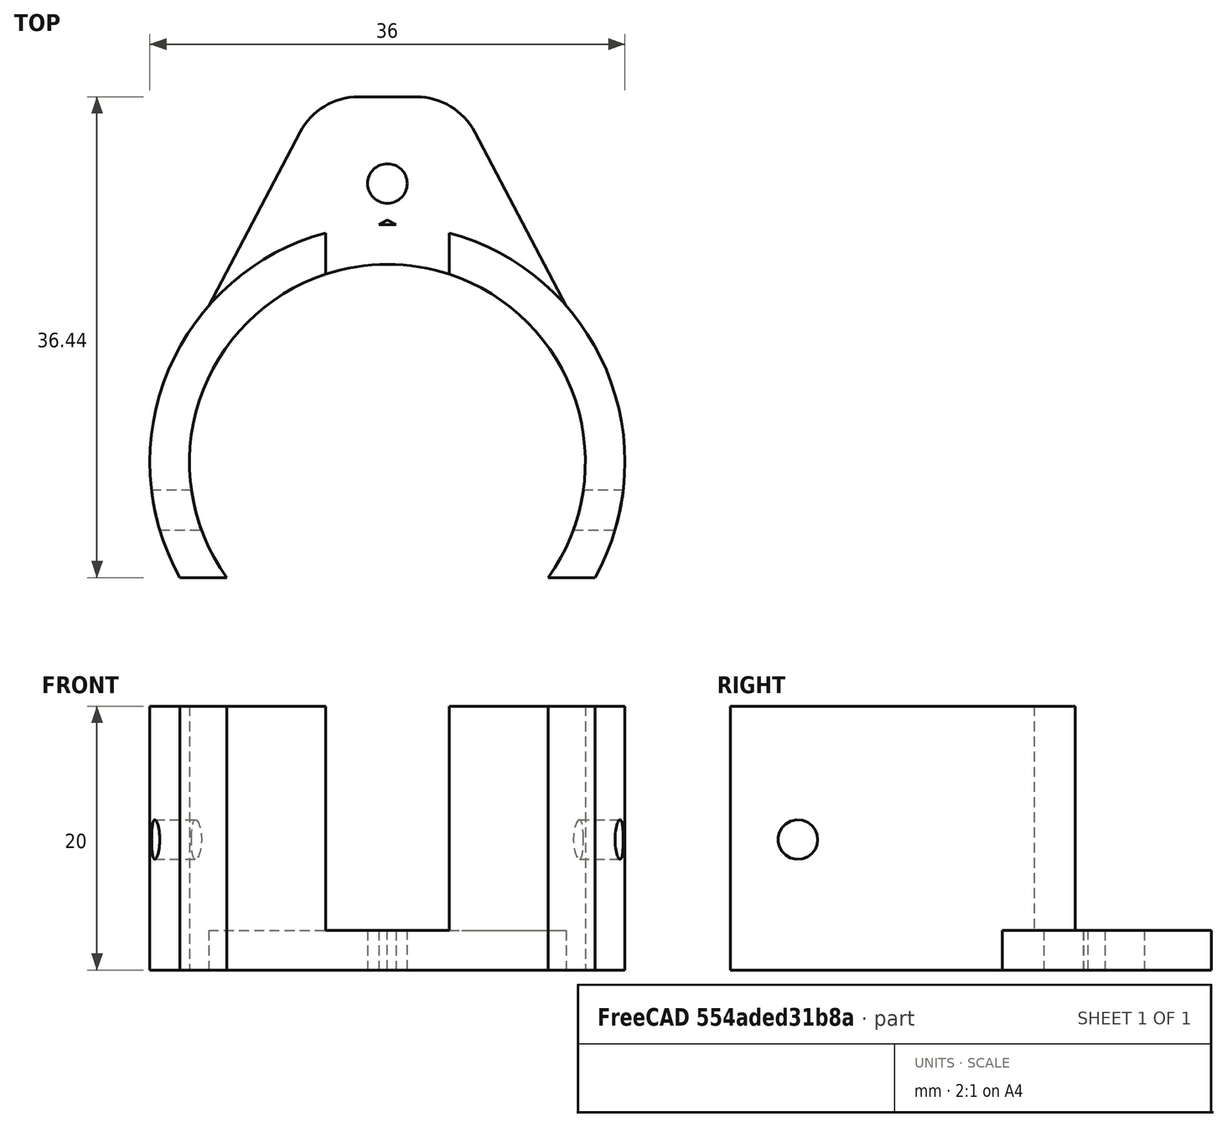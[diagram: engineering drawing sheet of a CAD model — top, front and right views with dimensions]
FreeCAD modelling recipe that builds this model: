
FCSTD DOCUMENT  (FreeCAD 0.19R24366 (Git))
Label: spool holder
License: All rights reserved
LicenseURL: http://en.wikipedia.org/wiki/All_rights_reserved
objects: Sketcher::SketchObject×5, PartDesign::Pocket×3, PartDesign::Pad×2, PartDesign::Fillet×2, Mesh::Feature×1, PartDesign::Body×1
note: 20 computed .brp shape members not serialized (recipe doc carries the construction recipe); baked Part::Feature solids carry a one-line shape summary decoded from their .brp

FEATURE [Mesh::Feature] spoolStand
FEATURE [Sketcher::SketchObject] Sketch
  FullyConstrained = false
  MapMode = 5
  Support = -> [XY_Plane]
  sketch-geometry (6):
    g0: ArcOfCircle CenterX=0 CenterY=3.63926 CenterZ=0 NormalX=0 NormalY=0 NormalZ=1 AngleXU=0 Radius=15 StartAngle=5.66017 EndAngle=10.0478
    g1: ArcOfCircle CenterX=0 CenterY=3.63926 CenterZ=0 NormalX=0 NormalY=0 NormalZ=1 AngleXU=0 Radius=18 StartAngle=5.7754 EndAngle=9.93256
    g2: LineSegment StartX=-15.7288 StartY=-5.11309 StartZ=0 EndX=-12.1818 EndY=-5.11309 EndZ=0
    g3: GeomPoint X=-12.1762 Y=-5.11309 Z=0
    g4: GeomPoint X=12.1761 Y=-5.11309 Z=0
    g5: LineSegment StartX=12.1818 StartY=-5.11309 StartZ=0 EndX=15.7288 EndY=-5.11309 EndZ=0
  constraints (11):
    c: PointOnObject(g0,g-2)
    c: Radius(g0) = 15
    c: Coincident(g1,g0)
    c: Horizontal(g2)
    c: PointOnObject(g3,g2)
    c: PointOnObject(g4,g2)
    c: Coincident(g1,g5)
    c: Coincident(g1,g2)
    c: Coincident(g2,g0)
    c: Coincident(g5,g0)
    c: Tangent(g2,g5)
FEATURE [PartDesign::Pad] Pad
  Direction = (1,1,1)
  Length = 20
  Length2 = 100
  Profile = -> Sketch
  Type = 0
FEATURE [Sketcher::SketchObject] Sketch002
  AttachmentOffset = pos=(0,0,3) rot=(0,0,1;0rad)
  FullyConstrained = false
  MapMode = 5
  Placement = pos=(0,0,3) rot=(0,0,1;0rad)
  Support = -> [XY_Plane]
  sketch-geometry (4):
    g0: LineSegment StartX=-4.69492 StartY=22 StartZ=0 EndX=4.69492 EndY=22 EndZ=0
    g1: LineSegment StartX=4.69492 StartY=22 StartZ=0 EndX=4.69492 EndY=16.8424 EndZ=0
    g2: LineSegment StartX=4.69492 StartY=16.8424 StartZ=0 EndX=-4.69492 EndY=16.8424 EndZ=0
    g3: LineSegment StartX=-4.69492 StartY=16.8424 StartZ=0 EndX=-4.69492 EndY=22 EndZ=0
  constraints (9):
    c: Coincident(g0,g1)
    c: Coincident(g1,g2)
    c: Coincident(g2,g3)
    c: Coincident(g3,g0)
    c: Horizontal(g2)
    c: Vertical(g1)
    c: Vertical(g3)
    c: DistanceY(g-1,g0) = 22
    c: Symmetric(g0,g0,g-2)
FEATURE [PartDesign::Pocket] Pocket
  BaseFeature = -> Pad
  Length = 17
  Length2 = 100
  Offset = 3
  Profile = -> Sketch002
  Reversed = true
  Type = 0
FEATURE [Sketcher::SketchObject] Sketch003
  FullyConstrained = false
  MapMode = 5
  Support = -> [XY_Plane]
  sketch-geometry (5):
    g0: LineSegment StartX=-14.5357 StartY=13.6078 StartZ=0 EndX=-5.21929 EndY=31.3309 EndZ=0
    g1: LineSegment StartX=-5.21929 StartY=31.3309 StartZ=0 EndX=5.21929 EndY=31.3309 EndZ=0
    g2: LineSegment StartX=5.21929 StartY=31.3309 StartZ=0 EndX=14.5357 EndY=13.6078 EndZ=0
    g3: LineSegment StartX=14.5357 StartY=13.6078 StartZ=0 EndX=0 EndY=22 EndZ=0
    g4: LineSegment StartX=0 StartY=22 StartZ=0 EndX=-14.5357 EndY=13.6078 EndZ=0
  constraints (12):
    c: Coincident(g0,g1)
    c: Horizontal(g1)
    c: Coincident(g1,g2)
    c: Coincident(g2,g3)
    c: PointOnObject(g3,g-2)
    c: Coincident(g3,g4)
    c: Coincident(g4,g0)
    c: Equal(g4,g3)
    c: Angle(g4,g-2) = 1.0472
    c: Angle(g-2,g3) = 1.0472
    c: DistanceY(g-1,g3) = 22
    c: Equal(g0,g2)
FEATURE [PartDesign::Pad] Pad002
  BaseFeature = -> Pocket
  Direction = (1,1,1)
  Length = 3
  Length2 = 100
  Profile = -> Sketch003
  Type = 0
FEATURE [Sketcher::SketchObject] Sketch004
  FullyConstrained = false
  MapMode = 5
  Support = -> [XY_Plane]
  sketch-geometry (1):
    g0: Circle CenterX=0 CenterY=24.7569 CenterZ=0 NormalX=0 NormalY=0 NormalZ=1 AngleXU=0 Radius=1.5
  constraints (2):
    c: PointOnObject(g0,g-2)
    c: Radius(g0) = 1.5
FEATURE [PartDesign::Pocket] Pocket001
  BaseFeature = -> Pad002
  Length = 5
  Length2 = 100
  Profile = -> Sketch004
  Reversed = true
  Type = 0
FEATURE [PartDesign::Fillet] Fillet
  Base = -> Pocket001 [Edge59]
  BaseFeature = -> Pocket001
  Radius = 5
  SupportTransform = false
FEATURE [PartDesign::Fillet] Fillet001
  Base = -> Fillet [Edge22]
  BaseFeature = -> Fillet
  Radius = 5
  SupportTransform = false
FEATURE [Sketcher::SketchObject] Sketch005
  FullyConstrained = false
  MapMode = 5
  Placement = pos=(0,0,0) rot=(0.57735,0.57735,0.57735;2.0944rad)
  Support = -> [YZ_Plane]
  sketch-geometry (1):
    g0: Circle CenterX=0 CenterY=9.89338 CenterZ=0 NormalX=0 NormalY=0 NormalZ=1 AngleXU=0 Radius=1.5
  constraints (2):
    c: PointOnObject(g0,g-2)
    c: Radius(g0) = 1.5
FEATURE [PartDesign::Pocket] Pocket002
  BaseFeature = -> Fillet001
  Length = 5
  Length2 = 100
  Midplane = true
  Profile = -> Sketch005
  Reversed = true
  Type = 1
FEATURE [PartDesign::Body] Body
  Group = -> [Sketch,Pad,Sketch002,Pocket,Sketch003,Pad002,Sketch004,Pocket001,Fillet,Fillet001,Sketch005,Pocket002]
  Origin = -> Origin
  Tip = -> Pocket002
